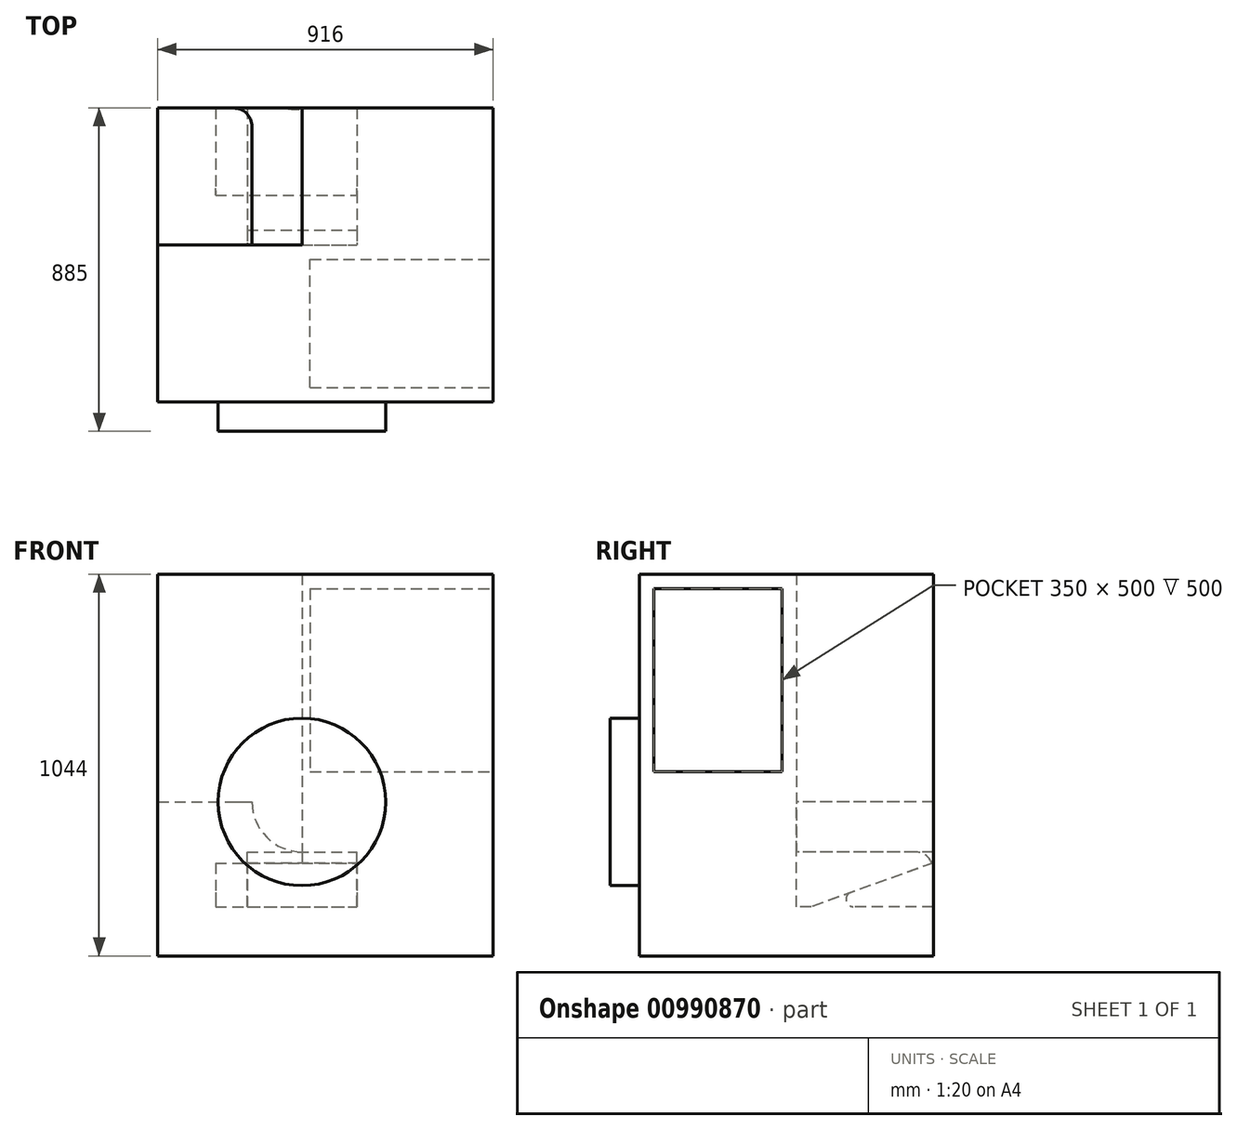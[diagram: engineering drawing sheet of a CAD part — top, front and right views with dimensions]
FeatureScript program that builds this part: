
annotation { "Feature Type Name" : "Feature", "Feature Type Description" : "" }
export const myFeature = defineFeature(function(context is Context, id is Id, definition is map)
    precondition{}
    {
        {
            var Q0;
            Q0=qCreatedBy(makeId("Top.planeOp"),FACE);
            var sketch = newSketch(context, id + "F0", { "sketchPlane" : qUnion([Q0])});
            skLineSegment(sketch, "E0.bottom", {"start": v(0, 0) * mm, "end": v(916, 0) * mm});
            skLineSegment(sketch, "E0.top", {"start": v(0, 430) * mm, "end": v(916, 430) * mm});
            skLineSegment(sketch, "E0.left", {"start": v(0, 0) * mm, "end": v(0, 430) * mm});
            skLineSegment(sketch, "E0.right", {"start": v(916, 0) * mm, "end": v(916, 430) * mm});
            skSolve(sketch);
        }
        {
            var Q0;
            Q0 = qSketchRegion(id + "F0", true);
            extrude(context, id + "F1", {"entities" : qUnion([Q0]), "depth" : 1044 * mm, "offsetDistance" : 25 * mm});
        }
        {
            var Q0;
            Q0=makeQuery(id+"F1.opExtrude","SWEPT_FACE",FACE,{"disambiguationData":[OSD([sQuery(id+"F0.wireOp",EDGE,"E0.bottom")])]});
            var sketch = newSketch(context, id + "F2", { "sketchPlane" : qUnion([Q0])});
            skLineSegment(sketch, "E1", {"start": v(-148.88, 421) * mm, "end": v(1037.26, 421) * mm});
            skLineSegment(sketch, "E2", {"start": v(394, 836.36) * mm, "end": v(394, 289.66) * mm});
            skCircle(sketch, "E3", {"center": v(394, 421) * mm, "radius": 229 * mm});
            skSolve(sketch);
        }
        {
            var Q0;
            {var subQ0=sQuery(id+"F2.wireOp",EDGE,"E1");var subQ1=makeQuery(id+"F2.imprint","INTERSECT",VERTEX,{"derivedFrom":[subQ0,sQuery(id+"F2.wireOp",EDGE,"E2")]});Q0=makeQuery(id+"F2.imprint","IMPRINT",FACE,{"disambiguationData":[TD([[makeQuery(id+"F2.imprint","IMPRINT",EDGE,{"disambiguationData":[TD([[subQ1,1.0]])],"derivedFrom":subQ0}),-1.0]])]});}
            var Q1;
            {var subQ0=sQuery(id+"F2.wireOp",EDGE,"E2");var subQ1=sQuery(id+"F2.wireOp",EDGE,"E1");var subQ2=makeQuery(id+"F2.imprint","INTERSECT",VERTEX,{"derivedFrom":[subQ1,subQ0]});Q1=makeQuery(id+"F2.imprint","IMPRINT",FACE,{"disambiguationData":[TD([[makeQuery(id+"F2.imprint","IMPRINT",EDGE,{"disambiguationData":[TD([[subQ2,1.0]])],"derivedFrom":subQ1}),1.0]])]});}
            var Q2;
            {var subQ0=sQuery(id+"F2.wireOp",EDGE,"E2");var subQ1=sQuery(id+"F2.wireOp",EDGE,"E1");var subQ2=makeQuery(id+"F2.imprint","INTERSECT",VERTEX,{"derivedFrom":[subQ1,subQ0]});Q2=makeQuery(id+"F2.imprint","IMPRINT",FACE,{"disambiguationData":[TD([[makeQuery(id+"F2.imprint","IMPRINT",EDGE,{"disambiguationData":[TD([[subQ2,-1.0]])],"derivedFrom":subQ1}),1.0]])]});}
            extrude(context, id + "F3", {"entities" : qUnion([Q0, Q1, Q2]), "operationType" : NewBodyOperationType.ADD, "depth" : 80 * mm, "offsetDistance" : 25 * mm});
        }
        {
            var Q0;
            Q0=makeQuery(id+"F1.opExtrude","SWEPT_FACE",FACE,{"disambiguationData":[OSD([sQuery(id+"F0.wireOp",EDGE,"E0.right")])]});
            var sketch = newSketch(context, id + "F4", { "sketchPlane" : qUnion([Q0])});
            skLineSegment(sketch, "E4.0", {"start": v(0, 1004) * mm, "end": v(430, 1004) * mm});
            skLineSegment(sketch, "E5.0", {"start": v(40, 1004) * mm, "end": v(40, 504) * mm});
            skLineSegment(sketch, "E6.0", {"start": v(390, 1004) * mm, "end": v(390, 504) * mm});
            skLineSegment(sketch, "E7.0", {"start": v(0, 504) * mm, "end": v(430, 504) * mm});
            skLineSegment(sketch, "E8.0", {"start": v(0, 464) * mm, "end": v(430, 464) * mm});
            skSolve(sketch);
        }
        {
            var Q0;
            {var subQ0=sQuery(id+"F4.wireOp",EDGE,"E5.0");Q0=makeQuery(id+"F4.imprint","IMPRINT",FACE,{"disambiguationData":[TD([[makeQuery(id+"F4.imprint","IMPRINT",EDGE,{"derivedFrom":subQ0}),1.0]])]});}
            extrude(context, id + "F5", {"entities" : qUnion([Q0]), "operationType" : NewBodyOperationType.REMOVE, "oppositeDirection" : true, "depth" : 500 * mm, "offsetDistance" : 25 * mm});
        }
        {
            var Q0;
            Q0=makeQuery(id+"F1.opExtrude","SWEPT_FACE",FACE,{"disambiguationData":[OSD([sQuery(id+"F0.wireOp",EDGE,"E0.top")])]});
            var sketch = newSketch(context, id + "F6", { "sketchPlane" : qUnion([Q0])});
            skLineSegment(sketch, "E9.0", {"start": v(0, 421) * mm, "end": v(-916, 421) * mm});
            skLineSegment(sketch, "E10.0", {"start": v(-394, 1044) * mm, "end": v(-394, 284.5) * mm});
            skCircle(sketch, "E11", {"center": v(-394, 421) * mm, "radius": 136.5 * mm});
            skSolve(sketch);
        }
        {
            var Q0;
            {var subQ0=sQuery(id+"F6.wireOp",EDGE,"E10.0");var subQ1=sQuery(id+"F6.wireOp",EDGE,"E9.0");var subQ2=makeQuery(id+"F6.imprint","INTERSECT",VERTEX,{"derivedFrom":[subQ1,subQ0]});Q0=makeQuery(id+"F6.imprint","IMPRINT",FACE,{"disambiguationData":[TD([[makeQuery(id+"F6.imprint","IMPRINT",EDGE,{"disambiguationData":[TD([[subQ2,-1.0]])],"derivedFrom":subQ1}),-1.0]])]});}
            var Q1;
            {var subQ0=sQuery(id+"F6.wireOp",EDGE,"E10.0");var subQ1=sQuery(id+"F6.wireOp",EDGE,"E9.0");var subQ2=makeQuery(id+"F6.imprint","INTERSECT",VERTEX,{"derivedFrom":[subQ1,subQ0]});Q1=makeQuery(id+"F6.imprint","IMPRINT",FACE,{"disambiguationData":[TD([[makeQuery(id+"F6.imprint","IMPRINT",EDGE,{"disambiguationData":[TD([[subQ2,-1.0]])],"derivedFrom":subQ1}),1.0]])]});}
            var Q2;
            {var subQ0=sQuery(id+"F6.wireOp",EDGE,"E11");var subQ1=sQuery(id+"F6.wireOp",EDGE,"E9.0");var subQ2=makeQuery(id+"F6.imprint","INTERSECT",VERTEX,{"disambiguationData":[OD(0.0)],"derivedFrom":[subQ1,subQ0]});Q2=makeQuery(id+"F6.imprint","IMPRINT",FACE,{"disambiguationData":[TD([[makeQuery(id+"F6.imprint","IMPRINT",EDGE,{"disambiguationData":[TD([[subQ2,-1.0]])],"derivedFrom":subQ1}),1.0]])]});}
            var Q3;
            {var subQ0=sQuery(id+"F6.wireOp",EDGE,"E11");var subQ1=sQuery(id+"F6.wireOp",EDGE,"E9.0");var subQ2=makeQuery(id+"F6.imprint","INTERSECT",VERTEX,{"disambiguationData":[OD(0.0)],"derivedFrom":[subQ1,subQ0]});Q3=makeQuery(id+"F6.imprint","IMPRINT",FACE,{"disambiguationData":[TD([[makeQuery(id+"F6.imprint","IMPRINT",EDGE,{"disambiguationData":[TD([[subQ2,-1.0]])],"derivedFrom":subQ1}),-1.0]])]});}
            extrude(context, id + "F7", {"entities" : qUnion([Q0, Q1, Q2, Q3]), "operationType" : NewBodyOperationType.ADD, "depth" : 374 * mm, "offsetDistance" : 25 * mm});
        }
        {
            var Q0;
            Q0=makeQuery(id+"F7.opExtrude","CAP_EDGE",EDGE,{"disambiguationData":[OSD([sQuery(id+"F6.wireOp",EDGE,"E11")])],"isStart":false});
            fillet(context, id + "F8", {"entities" : qUnion([Q0]), "radius" : 50 * mm, "tangentPropagation" : true, "allowEdgeOverflow" : false});
        }
        {
            var Q0;
            {var subQ4=sQuery(id+"F0.wireOp",EDGE,"E0.top");var subQ7=makeQuery(id+"F1.opExtrude","CAP_EDGE",EDGE,{"disambiguationData":[OSD([subQ4])],"isStart":true});Q0=makeQuery(id+"F6.imprint","IMPRINT",FACE,{"disambiguationData":[TD([[makeQuery(id+"F6.imprint","IMPRINT",EDGE,{"derivedFrom":subQ7}),-1.0]])]});}
            var sketch = newSketch(context, id + "F9", { "sketchPlane" : qUnion([Q0])});
            skLineSegment(sketch, "E12", {"start": v(0, 0) * mm, "end": v(0, 284.5) * mm});
            skLineSegment(sketch, "E13", {"start": v(-244, 134.5) * mm, "end": v(-544, 134.5) * mm});
            skLineSegment(sketch, "E14", {"start": v(-916, 134.5) * mm, "end": v(-916, 55.99) * mm});
            skLineSegment(sketch, "E15", {"start": v(-916, 55.99) * mm, "end": v(-394, 55.99) * mm});
            skLineSegment(sketch, "E16", {"start": v(-394, 55.99) * mm, "end": v(-394, 688.22) * mm});
            skLineSegment(sketch, "E17.0", {"start": v(-244, 134.5) * mm, "end": v(-244, 284.5) * mm});
            skLineSegment(sketch, "E18.0", {"start": v(-544, 134.5) * mm, "end": v(-544, 284.5) * mm});
            skLineSegment(sketch, "E19", {"start": v(-244, 284.5) * mm, "end": v(-544, 284.5) * mm});
            skSolve(sketch);
        }
        {
            var Q0;
            {var subQ0=sQuery(id+"F9.wireOp",EDGE,"E17.0");Q0=makeQuery(id+"F9.imprint","IMPRINT",FACE,{"disambiguationData":[TD([[makeQuery(id+"F9.imprint","IMPRINT",EDGE,{"derivedFrom":subQ0}),1.0]])]});}
            var Q1;
            {var subQ0=sQuery(id+"F9.wireOp",EDGE,"E18.0");Q1=makeQuery(id+"F9.imprint","IMPRINT",FACE,{"disambiguationData":[TD([[makeQuery(id+"F9.imprint","IMPRINT",EDGE,{"derivedFrom":subQ0}),-1.0]])]});}
            extrude(context, id + "F10", {"entities" : qUnion([Q0, Q1]), "depth" : 375 * mm, "offsetDistance" : 25 * mm});
        }
        {
            var Q0;
            Q0=makeQuery(id+"F10.opExtrude","SWEPT_FACE",FACE,{"disambiguationData":[OSD([sQuery(id+"F9.wireOp",EDGE,"E18.0")])]});
            var sketch = newSketch(context, id + "F11", { "sketchPlane" : qUnion([Q0])});
            skLineSegment(sketch, "E20", {"start": v(805, 254.5) * mm, "end": v(470, 134.5) * mm});
            skLineSegment(sketch, "E21", {"start": v(470, 134.5) * mm, "end": v(805, 134.5) * mm});
            skLineSegment(sketch, "E22", {"start": v(805, 134.5) * mm, "end": v(805, 254.5) * mm});
            skSolve(sketch);
        }
        {
            var Q0;
            Q0=makeQuery(id+"F11.imprint","IMPRINT",FACE,{"disambiguationData":[TD([[makeQuery(id+"F11.imprint","IMPRINT",EDGE,{"derivedFrom":sQuery(id+"F11.wireOp",EDGE,"E20")}),1.0]])]});
            extrude(context, id + "F12", {"entities" : qUnion([Q0]), "operationType" : NewBodyOperationType.REMOVE, "oppositeDirection" : true, "depth" : 386 * mm, "offsetDistance" : 25 * mm});
        }
        {
            var Q0;
            Q0=makeQuery(id+"F12.boolean.opBoolean","COPY",EDGE,{"derivedFrom":makeQuery(id+"F12.opExtrude","SWEPT_EDGE",EDGE,{"disambiguationData":[OSD([sQuery(id+"F9.wireOp",EDGE,"E13"),sQuery(id+"F9.wireOp",EDGE,"E18.0"),sQuery(id+"F11.wireOp",EDGE,"E20"),sQuery(id+"F11.wireOp",EDGE,"E21")])]})});
            var Q1;
            Q1=makeQuery(id+"F12.boolean.opBoolean","COPY",EDGE,{"derivedFrom":makeQuery(id+"F12.opExtrude","SWEPT_EDGE",EDGE,{"disambiguationData":[OSD([sQuery(id+"F9.wireOp",EDGE,"E18.0"),sQuery(id+"F11.wireOp",EDGE,"E20"),sQuery(id+"F11.wireOp",EDGE,"E22")])]})});
            fillet(context, id + "F13", {"entities" : qUnion([Q0, Q1]), "radius" : 20 * mm, "tangentPropagation" : true, "allowEdgeOverflow" : false});
        }
    });
